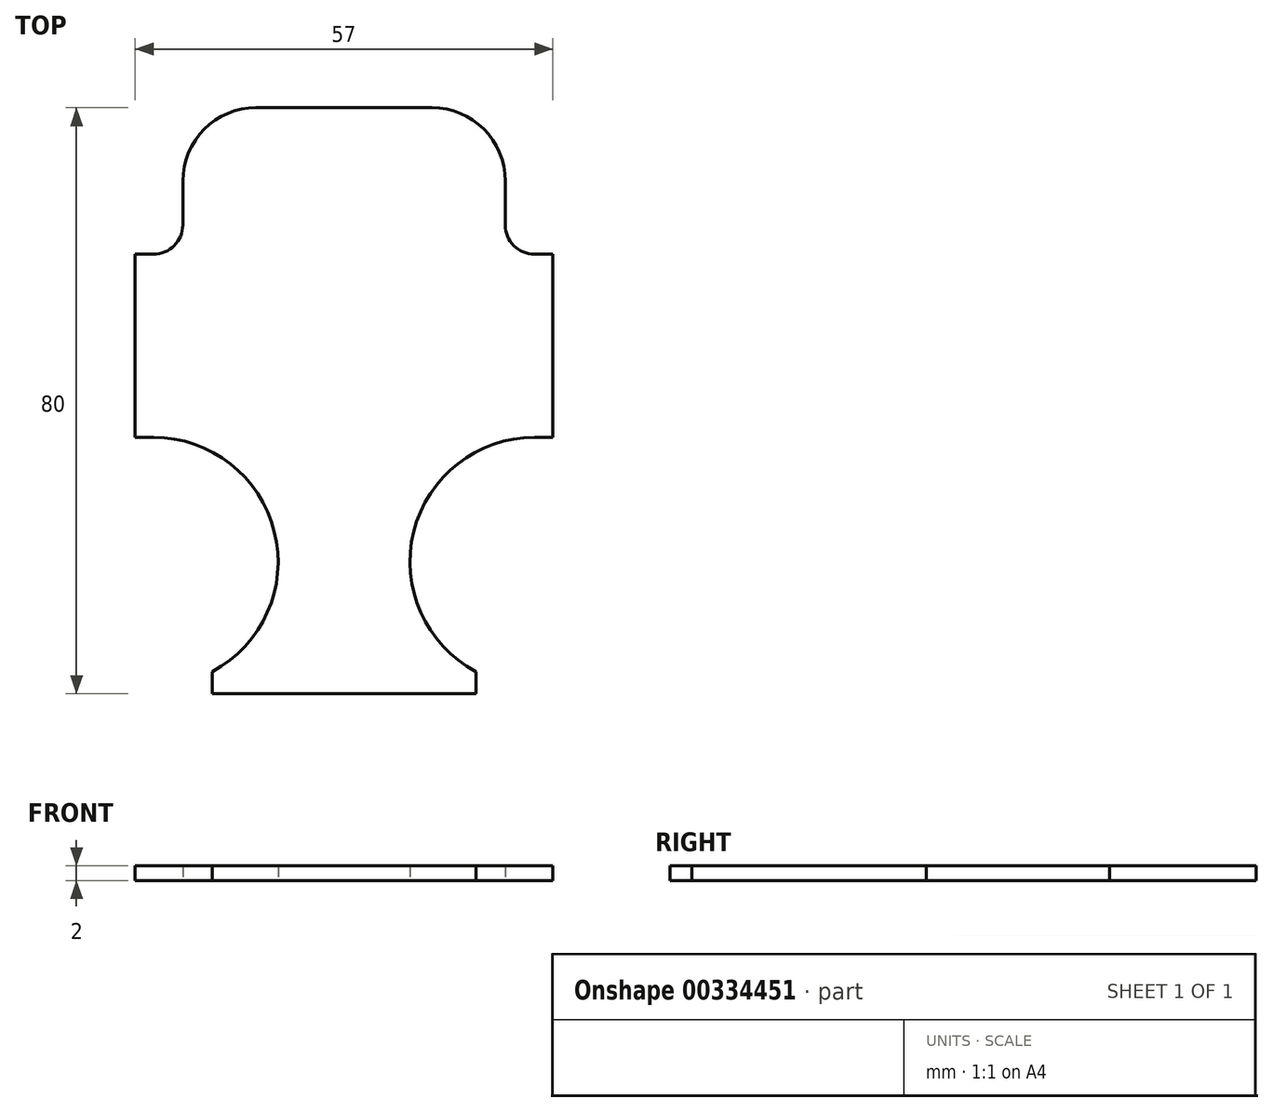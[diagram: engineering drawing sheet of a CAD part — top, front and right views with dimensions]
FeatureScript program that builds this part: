
annotation { "Feature Type Name" : "Feature", "Feature Type Description" : "" }
export const myFeature = defineFeature(function(context is Context, id is Id, definition is map)
    precondition{}
    {
        {
            var Q0;
            Q0=qCreatedBy(makeId("Top.planeOp"),FACE);
            var sketch = newSketch(context, id + "F0", { "sketchPlane" : qUnion([Q0])});
            skLineSegment(sketch, "E0", {"start": v(0, 38) * mm, "end": v(0, -42) * mm, "construction": true});
            skLineSegment(sketch, "E1", {"start": v(0, 38) * mm, "end": v(-12, 38) * mm});
            skArc(sketch, "E2", {"start": v(-12, 38) * mm, "mid": v(-19.07, 35.07) * mm, "end": v(-22, 28) * mm});
            skLineSegment(sketch, "E3", {"start": v(-22, 28) * mm, "end": v(-22, 22) * mm});
            skArc(sketch, "E4", {"start": v(-26, 18) * mm, "mid": v(-23.17, 19.17) * mm, "end": v(-22, 22) * mm});
            skLineSegment(sketch, "E5", {"start": v(-26, 18) * mm, "end": v(-28.5, 18) * mm});
            skLineSegment(sketch, "E6", {"start": v(-28.5, 18) * mm, "end": v(-28.5, -7) * mm});
            skLineSegment(sketch, "E7", {"start": v(-28.5, -7) * mm, "end": v(-26, -7) * mm});
            skArc(sketch, "E8", {"start": v(-18, -39) * mm, "mid": v(-9.5, -19.88) * mm, "end": v(-26, -7) * mm});
            skLineSegment(sketch, "E9", {"start": v(-18, -39) * mm, "end": v(-18, -42) * mm});
            skLineSegment(sketch, "E10", {"start": v(-18, -42) * mm, "end": v(0, -42) * mm});
            skLineSegment(sketch, "E11.MirrorCS", {"start": v(0, 38) * mm, "end": v(12, 38) * mm});
            skArc(sketch, "E12.MirrorCS", {"start": v(12, 38) * mm, "mid": v(19.07, 35.07) * mm, "end": v(22, 28) * mm});
            skLineSegment(sketch, "E13.MirrorCS", {"start": v(22, 28) * mm, "end": v(22, 22) * mm});
            skArc(sketch, "E14.MirrorCS", {"start": v(26, 18) * mm, "mid": v(23.17, 19.17) * mm, "end": v(22, 22) * mm});
            skLineSegment(sketch, "E15.MirrorCS", {"start": v(26, 18) * mm, "end": v(28.5, 18) * mm});
            skLineSegment(sketch, "E16.MirrorCS", {"start": v(28.5, 18) * mm, "end": v(28.5, -7) * mm});
            skLineSegment(sketch, "E17.MirrorCS", {"start": v(28.5, -7) * mm, "end": v(26, -7) * mm});
            skArc(sketch, "E18.MirrorCS", {"start": v(18, -39) * mm, "mid": v(9.5, -19.88) * mm, "end": v(26, -7) * mm});
            skLineSegment(sketch, "E19.MirrorCS", {"start": v(18, -39) * mm, "end": v(18, -42) * mm});
            skLineSegment(sketch, "E20.MirrorCS", {"start": v(18, -42) * mm, "end": v(0, -42) * mm});
            skSolve(sketch);
        }
        {
            var Q0;
            Q0=qSketchRegion(id+"F0",true);
            var Q1;
            Q1=makeQuery(id+"F0.imprint","IMPRINT",FACE,{"disambiguationData":[TD([[makeQuery(id+"F0.imprint","IMPRINT",EDGE,{"derivedFrom":sQuery(id+"F0.wireOp",EDGE,"E1")}),1.0]])]});
            extrude(context, id + "F1", {"entities" : qUnion([Q0, Q1]), "depth" : 2 * mm});
        }
    });
